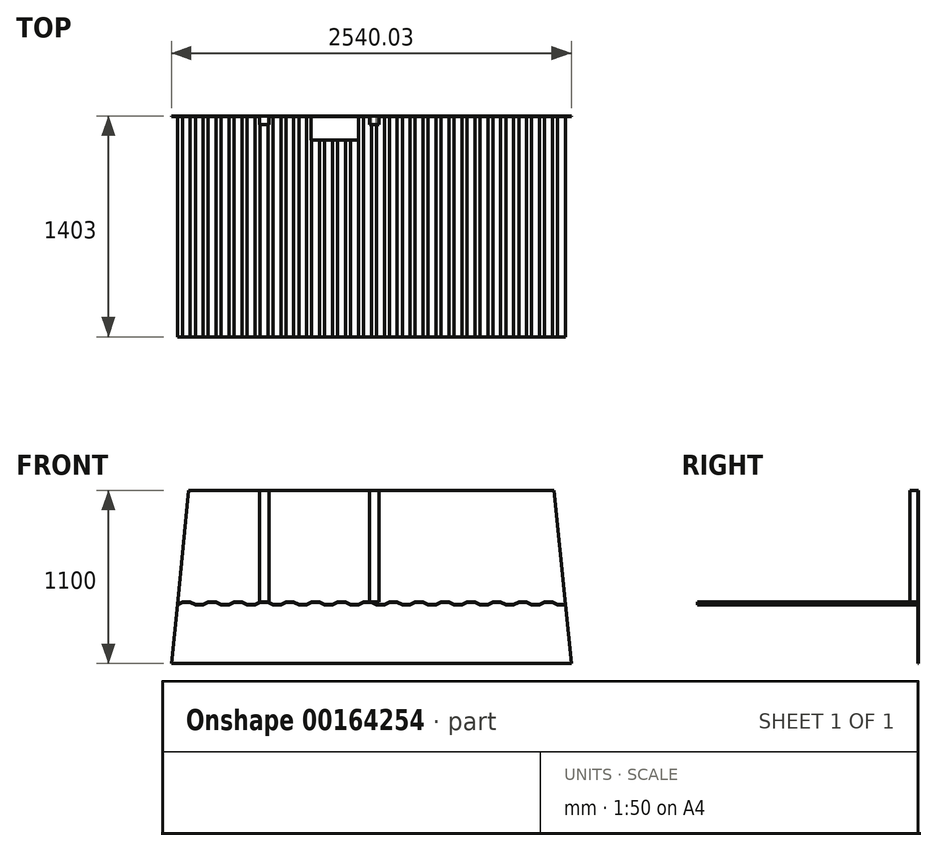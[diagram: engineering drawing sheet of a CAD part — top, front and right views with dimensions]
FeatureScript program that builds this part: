
annotation { "Feature Type Name" : "Feature", "Feature Type Description" : "" }
export const myFeature = defineFeature(function(context is Context, id is Id, definition is map)
    precondition{}
    {
        {
            var Q0;
            Q0=qCreatedBy(makeId("Front.planeOp"),FACE);
            var sketch = newSketch(context, id + "F0", { "sketchPlane" : qUnion([Q0])});
            skLineSegment(sketch, "E0", {"start": v(-539.28, 78.98) * mm, "end": v(-507.11, 93.98) * mm});
            skLineSegment(sketch, "E1", {"start": v(-507.11, 93.98) * mm, "end": v(-457.11, 93.98) * mm});
            skLineSegment(sketch, "E2", {"start": v(-457.11, 93.98) * mm, "end": v(-424.94, 78.98) * mm});
            skLineSegment(sketch, "E3", {"start": v(-424.94, 78.98) * mm, "end": v(-374.94, 78.98) * mm});
            skLineSegment(sketch, "E4.1.0.0", {"start": v(-260.6, 78.98) * mm, "end": v(-210.6, 78.98) * mm});
            skLineSegment(sketch, "E4.1.0.1", {"start": v(-292.78, 93.98) * mm, "end": v(-260.6, 78.98) * mm});
            skLineSegment(sketch, "E4.1.0.2", {"start": v(-342.78, 93.98) * mm, "end": v(-292.78, 93.98) * mm});
            skLineSegment(sketch, "E4.1.0.3", {"start": v(-374.94, 78.98) * mm, "end": v(-342.78, 93.98) * mm});
            skLineSegment(sketch, "E4.2.0.0", {"start": v(-96.27, 78.98) * mm, "end": v(-46.27, 78.98) * mm});
            skLineSegment(sketch, "E4.2.0.1", {"start": v(-128.44, 93.98) * mm, "end": v(-96.27, 78.98) * mm});
            skLineSegment(sketch, "E4.2.0.2", {"start": v(-178.44, 93.98) * mm, "end": v(-128.44, 93.98) * mm});
            skLineSegment(sketch, "E4.2.0.3", {"start": v(-210.6, 78.98) * mm, "end": v(-178.44, 93.98) * mm});
            skLineSegment(sketch, "E4.direction1", {"start": v(-539.28, 78.98) * mm, "end": v(-374.94, 78.98) * mm, "construction": true});
            skLineSegment(sketch, "E5.0.3.0", {"start": v(68.06, 78.98) * mm, "end": v(118.06, 78.98) * mm});
            skLineSegment(sketch, "E5.3.3.0", {"start": v(35.9, 93.98) * mm, "end": v(68.06, 78.98) * mm});
            skLineSegment(sketch, "E5.6.3.0", {"start": v(-14.1, 93.98) * mm, "end": v(35.9, 93.98) * mm});
            skLineSegment(sketch, "E5.9.3.0", {"start": v(-46.27, 78.98) * mm, "end": v(-14.1, 93.98) * mm});
            skLineSegment(sketch, "E5.0.4.0", {"start": v(232.4, 78.98) * mm, "end": v(282.4, 78.98) * mm});
            skLineSegment(sketch, "E5.3.4.0", {"start": v(200.23, 93.98) * mm, "end": v(232.4, 78.98) * mm});
            skLineSegment(sketch, "E5.6.4.0", {"start": v(150.23, 93.98) * mm, "end": v(200.23, 93.98) * mm});
            skLineSegment(sketch, "E5.9.4.0", {"start": v(118.06, 78.98) * mm, "end": v(150.23, 93.98) * mm});
            skLineSegment(sketch, "E5.0.5.0", {"start": v(396.73, 78.98) * mm, "end": v(446.73, 78.98) * mm});
            skLineSegment(sketch, "E5.3.5.0", {"start": v(364.56, 93.98) * mm, "end": v(396.73, 78.98) * mm});
            skLineSegment(sketch, "E5.6.5.0", {"start": v(314.56, 93.98) * mm, "end": v(364.56, 93.98) * mm});
            skLineSegment(sketch, "E5.9.5.0", {"start": v(282.4, 78.98) * mm, "end": v(314.56, 93.98) * mm});
            skLineSegment(sketch, "E5.0.6.0", {"start": v(561.07, 78.98) * mm, "end": v(611.07, 78.98) * mm});
            skLineSegment(sketch, "E5.3.6.0", {"start": v(528.9, 93.98) * mm, "end": v(561.07, 78.98) * mm});
            skLineSegment(sketch, "E5.6.6.0", {"start": v(478.9, 93.98) * mm, "end": v(528.9, 93.98) * mm});
            skLineSegment(sketch, "E5.9.6.0", {"start": v(446.73, 78.98) * mm, "end": v(478.9, 93.98) * mm});
            skLineSegment(sketch, "E5.0.7.0", {"start": v(725.4, 78.98) * mm, "end": v(775.4, 78.98) * mm});
            skLineSegment(sketch, "E5.3.7.0", {"start": v(693.23, 93.98) * mm, "end": v(725.4, 78.98) * mm});
            skLineSegment(sketch, "E5.6.7.0", {"start": v(643.23, 93.98) * mm, "end": v(693.23, 93.98) * mm});
            skLineSegment(sketch, "E5.9.7.0", {"start": v(611.07, 78.98) * mm, "end": v(643.23, 93.98) * mm});
            skLineSegment(sketch, "E5.0.8.0", {"start": v(889.74, 78.98) * mm, "end": v(939.74, 78.98) * mm});
            skLineSegment(sketch, "E5.3.8.0", {"start": v(857.57, 93.98) * mm, "end": v(889.74, 78.98) * mm});
            skLineSegment(sketch, "E5.6.8.0", {"start": v(807.57, 93.98) * mm, "end": v(857.57, 93.98) * mm});
            skLineSegment(sketch, "E5.9.8.0", {"start": v(775.4, 78.98) * mm, "end": v(807.57, 93.98) * mm});
            skLineSegment(sketch, "E5.0.9.0", {"start": v(1054.07, 78.98) * mm, "end": v(1104.07, 78.98) * mm});
            skLineSegment(sketch, "E5.3.9.0", {"start": v(1021.9, 93.98) * mm, "end": v(1054.07, 78.98) * mm});
            skLineSegment(sketch, "E5.6.9.0", {"start": v(971.9, 93.98) * mm, "end": v(1021.9, 93.98) * mm});
            skLineSegment(sketch, "E5.9.9.0", {"start": v(939.74, 78.98) * mm, "end": v(971.9, 93.98) * mm});
            skLineSegment(sketch, "E6.0.10.0", {"start": v(1218.4, 78.98) * mm, "end": v(1268.4, 78.98) * mm});
            skLineSegment(sketch, "E6.3.10.0", {"start": v(1186.24, 93.98) * mm, "end": v(1218.4, 78.98) * mm});
            skLineSegment(sketch, "E6.6.10.0", {"start": v(1136.24, 93.98) * mm, "end": v(1186.24, 93.98) * mm});
            skLineSegment(sketch, "E6.9.10.0", {"start": v(1104.07, 78.98) * mm, "end": v(1136.24, 93.98) * mm});
            skLineSegment(sketch, "E6.0.11.0", {"start": v(1382.74, 78.98) * mm, "end": v(1432.74, 78.98) * mm});
            skLineSegment(sketch, "E6.3.11.0", {"start": v(1350.57, 93.98) * mm, "end": v(1382.74, 78.98) * mm});
            skLineSegment(sketch, "E6.6.11.0", {"start": v(1300.57, 93.98) * mm, "end": v(1350.57, 93.98) * mm});
            skLineSegment(sketch, "E6.9.11.0", {"start": v(1268.4, 78.98) * mm, "end": v(1300.57, 93.98) * mm});
            skLineSegment(sketch, "E6.0.12.0", {"start": v(1547.08, 78.98) * mm, "end": v(1597.08, 78.98) * mm});
            skLineSegment(sketch, "E6.3.12.0", {"start": v(1514.9, 93.98) * mm, "end": v(1547.08, 78.98) * mm});
            skLineSegment(sketch, "E6.6.12.0", {"start": v(1464.9, 93.98) * mm, "end": v(1514.9, 93.98) * mm});
            skLineSegment(sketch, "E6.9.12.0", {"start": v(1432.74, 78.98) * mm, "end": v(1464.9, 93.98) * mm});
            skLineSegment(sketch, "E6.0.13.0", {"start": v(1711.41, 78.98) * mm, "end": v(1761.41, 78.98) * mm});
            skLineSegment(sketch, "E6.3.13.0", {"start": v(1679.24, 93.98) * mm, "end": v(1711.41, 78.98) * mm});
            skLineSegment(sketch, "E6.6.13.0", {"start": v(1629.24, 93.98) * mm, "end": v(1679.24, 93.98) * mm});
            skLineSegment(sketch, "E6.9.13.0", {"start": v(1597.08, 78.98) * mm, "end": v(1629.24, 93.98) * mm});
            skLineSegment(sketch, "E6.0.14.0", {"start": v(1875.75, 78.98) * mm, "end": v(1925.75, 78.98) * mm});
            skLineSegment(sketch, "E6.3.14.0", {"start": v(1843.58, 93.98) * mm, "end": v(1875.75, 78.98) * mm});
            skLineSegment(sketch, "E6.6.14.0", {"start": v(1793.58, 93.98) * mm, "end": v(1843.58, 93.98) * mm});
            skLineSegment(sketch, "E6.9.14.0", {"start": v(1761.41, 78.98) * mm, "end": v(1793.58, 93.98) * mm});
            skLineSegment(sketch, "E7", {"start": v(-539.28, 75.98) * mm, "end": v(-507.11, 90.98) * mm});
            skLineSegment(sketch, "E8", {"start": v(-507.11, 90.98) * mm, "end": v(-457.11, 90.98) * mm});
            skLineSegment(sketch, "E9", {"start": v(-457.11, 90.98) * mm, "end": v(-424.94, 75.98) * mm});
            skLineSegment(sketch, "E10", {"start": v(-424.94, 75.98) * mm, "end": v(-374.94, 75.98) * mm});
            skLineSegment(sketch, "E11.1.0.0", {"start": v(-260.6, 75.98) * mm, "end": v(-210.6, 75.98) * mm});
            skLineSegment(sketch, "E11.1.0.1", {"start": v(-292.78, 90.98) * mm, "end": v(-260.6, 75.98) * mm});
            skLineSegment(sketch, "E11.1.0.2", {"start": v(-342.78, 90.98) * mm, "end": v(-292.78, 90.98) * mm});
            skLineSegment(sketch, "E11.1.0.3", {"start": v(-374.94, 75.98) * mm, "end": v(-342.78, 90.98) * mm});
            skLineSegment(sketch, "E11.2.0.0", {"start": v(-96.27, 75.98) * mm, "end": v(-46.27, 75.98) * mm});
            skLineSegment(sketch, "E11.2.0.1", {"start": v(-128.44, 90.98) * mm, "end": v(-96.27, 75.98) * mm});
            skLineSegment(sketch, "E11.2.0.2", {"start": v(-178.44, 90.98) * mm, "end": v(-128.44, 90.98) * mm});
            skLineSegment(sketch, "E11.2.0.3", {"start": v(-210.6, 75.98) * mm, "end": v(-178.44, 90.98) * mm});
            skLineSegment(sketch, "E11.direction1", {"start": v(-539.28, 75.98) * mm, "end": v(-374.94, 75.98) * mm, "construction": true});
            skLineSegment(sketch, "E12.0.3.0", {"start": v(68.06, 75.98) * mm, "end": v(118.06, 75.98) * mm});
            skLineSegment(sketch, "E12.3.3.0", {"start": v(35.9, 90.98) * mm, "end": v(68.06, 75.98) * mm});
            skLineSegment(sketch, "E12.6.3.0", {"start": v(-14.1, 90.98) * mm, "end": v(35.9, 90.98) * mm});
            skLineSegment(sketch, "E12.9.3.0", {"start": v(-46.27, 75.98) * mm, "end": v(-14.1, 90.98) * mm});
            skLineSegment(sketch, "E12.0.4.0", {"start": v(232.4, 75.98) * mm, "end": v(282.4, 75.98) * mm});
            skLineSegment(sketch, "E12.3.4.0", {"start": v(200.23, 90.98) * mm, "end": v(232.4, 75.98) * mm});
            skLineSegment(sketch, "E12.6.4.0", {"start": v(150.23, 90.98) * mm, "end": v(200.23, 90.98) * mm});
            skLineSegment(sketch, "E12.9.4.0", {"start": v(118.06, 75.98) * mm, "end": v(150.23, 90.98) * mm});
            skLineSegment(sketch, "E12.0.5.0", {"start": v(396.73, 75.98) * mm, "end": v(446.73, 75.98) * mm});
            skLineSegment(sketch, "E12.3.5.0", {"start": v(364.56, 90.98) * mm, "end": v(396.73, 75.98) * mm});
            skLineSegment(sketch, "E12.6.5.0", {"start": v(314.56, 90.98) * mm, "end": v(364.56, 90.98) * mm});
            skLineSegment(sketch, "E12.9.5.0", {"start": v(282.4, 75.98) * mm, "end": v(314.56, 90.98) * mm});
            skLineSegment(sketch, "E12.0.6.0", {"start": v(561.07, 75.98) * mm, "end": v(611.07, 75.98) * mm});
            skLineSegment(sketch, "E12.3.6.0", {"start": v(528.9, 90.98) * mm, "end": v(561.07, 75.98) * mm});
            skLineSegment(sketch, "E12.6.6.0", {"start": v(478.9, 90.98) * mm, "end": v(528.9, 90.98) * mm});
            skLineSegment(sketch, "E12.9.6.0", {"start": v(446.73, 75.98) * mm, "end": v(478.9, 90.98) * mm});
            skLineSegment(sketch, "E12.0.7.0", {"start": v(725.4, 75.98) * mm, "end": v(775.4, 75.98) * mm});
            skLineSegment(sketch, "E12.3.7.0", {"start": v(693.23, 90.98) * mm, "end": v(725.4, 75.98) * mm});
            skLineSegment(sketch, "E12.6.7.0", {"start": v(643.23, 90.98) * mm, "end": v(693.23, 90.98) * mm});
            skLineSegment(sketch, "E12.9.7.0", {"start": v(611.07, 75.98) * mm, "end": v(643.23, 90.98) * mm});
            skLineSegment(sketch, "E12.0.8.0", {"start": v(889.74, 75.98) * mm, "end": v(939.74, 75.98) * mm});
            skLineSegment(sketch, "E12.3.8.0", {"start": v(857.57, 90.98) * mm, "end": v(889.74, 75.98) * mm});
            skLineSegment(sketch, "E12.6.8.0", {"start": v(807.57, 90.98) * mm, "end": v(857.57, 90.98) * mm});
            skLineSegment(sketch, "E12.9.8.0", {"start": v(775.4, 75.98) * mm, "end": v(807.57, 90.98) * mm});
            skLineSegment(sketch, "E12.0.9.0", {"start": v(1054.07, 75.98) * mm, "end": v(1104.07, 75.98) * mm});
            skLineSegment(sketch, "E12.3.9.0", {"start": v(1021.9, 90.98) * mm, "end": v(1054.07, 75.98) * mm});
            skLineSegment(sketch, "E12.6.9.0", {"start": v(971.9, 90.98) * mm, "end": v(1021.9, 90.98) * mm});
            skLineSegment(sketch, "E12.9.9.0", {"start": v(939.74, 75.98) * mm, "end": v(971.9, 90.98) * mm});
            skLineSegment(sketch, "E13", {"start": v(1925.75, 78.98) * mm, "end": v(1925.75, 75.98) * mm});
            skLineSegment(sketch, "E14", {"start": v(-539.28, 78.98) * mm, "end": v(-539.28, 75.98) * mm});
            skLineSegment(sketch, "E15.0.10.0", {"start": v(1218.4, 75.98) * mm, "end": v(1268.4, 75.98) * mm});
            skLineSegment(sketch, "E15.3.10.0", {"start": v(1186.24, 90.98) * mm, "end": v(1218.4, 75.98) * mm});
            skLineSegment(sketch, "E15.6.10.0", {"start": v(1136.24, 90.98) * mm, "end": v(1186.24, 90.98) * mm});
            skLineSegment(sketch, "E15.9.10.0", {"start": v(1104.07, 75.98) * mm, "end": v(1136.24, 90.98) * mm});
            skLineSegment(sketch, "E15.0.11.0", {"start": v(1382.74, 75.98) * mm, "end": v(1432.74, 75.98) * mm});
            skLineSegment(sketch, "E15.3.11.0", {"start": v(1350.57, 90.98) * mm, "end": v(1382.74, 75.98) * mm});
            skLineSegment(sketch, "E15.6.11.0", {"start": v(1300.57, 90.98) * mm, "end": v(1350.57, 90.98) * mm});
            skLineSegment(sketch, "E15.9.11.0", {"start": v(1268.4, 75.98) * mm, "end": v(1300.57, 90.98) * mm});
            skLineSegment(sketch, "E15.0.12.0", {"start": v(1547.08, 75.98) * mm, "end": v(1597.08, 75.98) * mm});
            skLineSegment(sketch, "E15.3.12.0", {"start": v(1514.9, 90.98) * mm, "end": v(1547.08, 75.98) * mm});
            skLineSegment(sketch, "E15.6.12.0", {"start": v(1464.9, 90.98) * mm, "end": v(1514.9, 90.98) * mm});
            skLineSegment(sketch, "E15.9.12.0", {"start": v(1432.74, 75.98) * mm, "end": v(1464.9, 90.98) * mm});
            skLineSegment(sketch, "E15.0.13.0", {"start": v(1711.41, 75.98) * mm, "end": v(1761.41, 75.98) * mm});
            skLineSegment(sketch, "E15.3.13.0", {"start": v(1679.24, 90.98) * mm, "end": v(1711.41, 75.98) * mm});
            skLineSegment(sketch, "E15.6.13.0", {"start": v(1629.24, 90.98) * mm, "end": v(1679.24, 90.98) * mm});
            skLineSegment(sketch, "E15.9.13.0", {"start": v(1597.08, 75.98) * mm, "end": v(1629.24, 90.98) * mm});
            skLineSegment(sketch, "E15.0.14.0", {"start": v(1875.75, 75.98) * mm, "end": v(1925.75, 75.98) * mm});
            skLineSegment(sketch, "E15.3.14.0", {"start": v(1843.58, 90.98) * mm, "end": v(1875.75, 75.98) * mm});
            skLineSegment(sketch, "E15.6.14.0", {"start": v(1793.58, 90.98) * mm, "end": v(1843.58, 90.98) * mm});
            skLineSegment(sketch, "E15.9.14.0", {"start": v(1761.41, 75.98) * mm, "end": v(1793.58, 90.98) * mm});
            skSolve(sketch);
        }
        {
            var Q0;
            Q0 = qSketchRegion(id + "F0", true);
            extrude(context, id + "F1", {"entities" : qUnion([Q0]), "depth" : 1400 * mm});
        }
        {
            var Q0;
            Q0=qCreatedBy(makeId("Top.planeOp"),FACE);
            var sketch = newSketch(context, id + "F2", { "sketchPlane" : qUnion([Q0])});
            skLineSegment(sketch, "E16.bottom", {"start": v(310.72, 50) * mm, "end": v(610.72, 50) * mm});
            skLineSegment(sketch, "E16.top", {"start": v(310.72, -150) * mm, "end": v(610.72, -150) * mm});
            skLineSegment(sketch, "E16.left", {"start": v(310.72, 50) * mm, "end": v(310.72, -150) * mm});
            skLineSegment(sketch, "E16.right", {"start": v(610.72, 50) * mm, "end": v(610.72, -150) * mm});
            skSolve(sketch);
        }
        {
            var Q0;
            Q0 = qSketchRegion(id + "F2", true);
            extrude(context, id + "F3", {"entities" : qUnion([Q0]), "operationType" : NewBodyOperationType.REMOVE, "endBound" : BoundingType.THROUGH_ALL, "depth" : 25 * mm});
        }
        {
            var Q0;
            Q0=qCreatedBy(makeId("Front.planeOp"),FACE);
            var sketch = newSketch(context, id + "F4", { "sketchPlane" : qUnion([Q0])});
            skLineSegment(sketch, "E17.bottom", {"start": v(-576.78, -296.02) * mm, "end": v(1963.25, -296.02) * mm});
            skLineSegment(sketch, "E17.top", {"start": v(-466.78, 803.98) * mm, "end": v(1853.25, 803.98) * mm});
            skLineSegment(sketch, "E17.left", {"start": v(-576.78, -296.02) * mm, "end": v(-466.78, 803.98) * mm});
            skLineSegment(sketch, "E17.right", {"start": v(1963.25, -296.02) * mm, "end": v(1853.25, 803.98) * mm});
            skSolve(sketch);
        }
        {
            var Q0;
            Q0 = qSketchRegion(id + "F4", true);
            extrude(context, id + "F5", {"entities" : qUnion([Q0]), "operationType" : NewBodyOperationType.ADD, "oppositeDirection" : true, "depth" : 3 * mm});
        }
        {
            var Q0;
            Q0=qCreatedBy(makeId("Front.planeOp"),FACE);
            var sketch = newSketch(context, id + "F6", { "sketchPlane" : qUnion([Q0])});
            skLineSegment(sketch, "E18.bottom", {"start": v(-18.28, 803.98) * mm, "end": v(41.72, 803.98) * mm});
            skLineSegment(sketch, "E18.top", {"start": v(-18.28, 93.98) * mm, "end": v(41.72, 93.98) * mm});
            skLineSegment(sketch, "E18.left", {"start": v(-18.28, 803.98) * mm, "end": v(-18.28, 93.98) * mm});
            skLineSegment(sketch, "E18.right", {"start": v(41.72, 803.98) * mm, "end": v(41.72, 93.98) * mm});
            skSolve(sketch);
        }
        {
            var Q0;
            Q0=makeQuery(id+"F6.imprint","IMPRINT",FACE,{"disambiguationData":[TD([[makeQuery(id+"F6.imprint","IMPRINT",EDGE,{"derivedFrom":sQuery(id+"F6.wireOp",EDGE,"E18.bottom")}),-1.0]])]});
            extrude(context, id + "F7", {"entities" : qUnion([Q0]), "operationType" : NewBodyOperationType.ADD, "depth" : 50 * mm});
        }
        {
            var Q0;
            {var subQ32=sQuery(id+"F0.wireOp",EDGE,"E5.0.3.0");var subQ33=makeQuery(id+"F1.opExtrude","SWEPT_FACE",FACE,{"disambiguationData":[OSD([subQ32])]});var subQ83=sQuery(id+"F0.wireOp",EDGE,"E1");var subQ96=sQuery(id+"F4.wireOp",EDGE,"E17.right");var subQ110=sQuery(id+"F4.wireOp",EDGE,"E17.top");var subQ112=sQuery(id+"F4.wireOp",EDGE,"E17.left");var subQ113=makeQuery(id+"F5.opExtrude","CAP_FACE",FACE,{"disambiguationData":[OSD([sQuery(id+"F4.wireOp",EDGE,"E17.bottom"),subQ110,subQ112,subQ96])],"isStart":true});Q0=makeQuery(id+"F7.boolean.opBoolean","SPLIT",FACE,{"disambiguationData":[TD([subQ33])],"derivedFrom":makeQuery(id+"F5.boolean.opBoolean","SPLIT",FACE,{"disambiguationData":[TD([makeQuery(id+"F1.opExtrude","SWEPT_FACE",FACE,{"disambiguationData":[OSD([subQ83])]})])],"derivedFrom":subQ113})});}
            var sketch = newSketch(context, id + "F8", { "sketchPlane" : qUnion([Q0])});
            skLineSegment(sketch, "E19.bottom", {"start": v(681.72, 803.98) * mm, "end": v(741.72, 803.98) * mm});
            skLineSegment(sketch, "E19.top", {"start": v(681.72, 93.98) * mm, "end": v(741.72, 93.98) * mm});
            skLineSegment(sketch, "E19.left", {"start": v(681.72, 803.98) * mm, "end": v(681.72, 93.98) * mm});
            skLineSegment(sketch, "E19.right", {"start": v(741.72, 803.98) * mm, "end": v(741.72, 93.98) * mm});
            skSolve(sketch);
        }
        {
            var Q0;
            Q0 = qSketchRegion(id + "F8", true);
            extrude(context, id + "F9", {"entities" : qUnion([Q0]), "operationType" : NewBodyOperationType.ADD, "depth" : 50 * mm});
        }
    });
